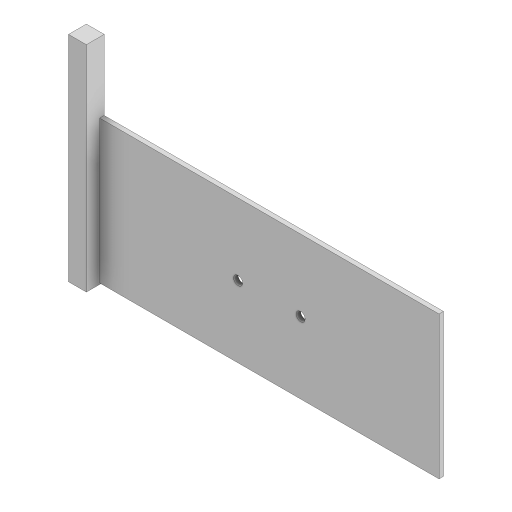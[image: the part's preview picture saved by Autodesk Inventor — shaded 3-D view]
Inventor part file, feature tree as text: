
AUTODESK INVENTOR PART (.ipt)
format: ipt  version: 2024.2 (Build 282272000, 272)  size: 104,448 bytes
history: native  units: in
note: dims shown in document units (in); Inventor stores cm internally (conversion verified against a paired STEP export)
features: extrude x2, sketch x2
ambient origin geometry x8: Origin, YZ Plane, XZ Plane, XY Plane, X Axis, Y Axis, Z Axis, Center Point
bodies: Solid1 (feature_tree)
feature tree (4):
  extrude  "Extrusion1"  Depth=4.0in
  extrude  "Extrusion2"  Depth=0.5in
  sketch  "Sketch1"  dims[d0=9.5in d1=4.0in]
  sketch  "Sketch2"  dims[d2=0.25in d3=0.25in d4=1.75in d5=3.875in d6=2.0in d7=0.125in d8=0.0in d9=0.5in d10=6.0in d11=0.0in d12=0.5in d13=0.0in]
